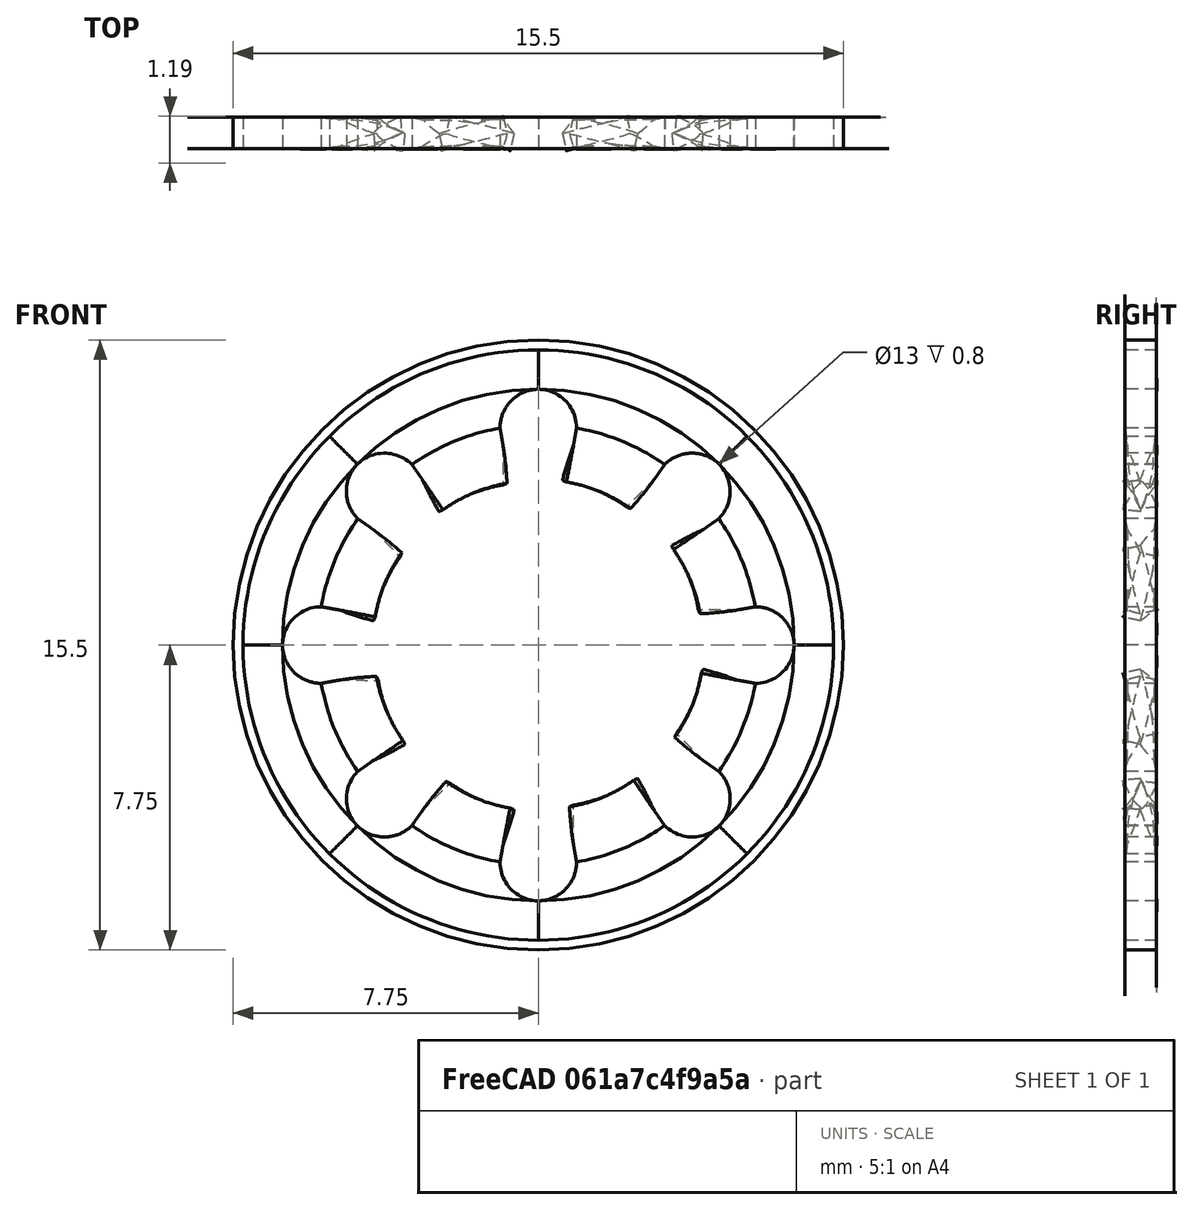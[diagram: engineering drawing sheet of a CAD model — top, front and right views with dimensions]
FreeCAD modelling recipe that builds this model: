
FCSTD DOCUMENT  (FreeCAD 0.19R24267 +99 (Git))
Label: Assembly TR Fastenings Ltd-M8 Internal Toothed Washer DIN 6797J
License: All rights reserved
LicenseURL: http://en.wikipedia.org/wiki/All_rights_reserved
objects: Part::Feature×1, Sketcher::SketchObject×1, PartDesign::Pad×1, PartDesign::Body×1
note: 5 computed .brp shape members not serialized (recipe doc carries the construction recipe); baked Part::Feature solids carry a one-line shape summary decoded from their .brp

FEATURE [Part::Feature] Part__Feature  label="TR Fastenings Ltd-M8"
  shape: bbox 19.22 x 1.686 x 19.22 mm, 104 faces, 8 solids (baked)
FEATURE [Sketcher::SketchObject] Sketch
  FullyConstrained = true
  MapMode = 5
  Placement = pos=(0,0,0) rot=(1,0,0;1.5708rad)
  Support = -> [XZ_Plane]
  sketch-geometry (2):
    g0: Circle CenterX=0 CenterY=0 CenterZ=0 NormalX=0 NormalY=0 NormalZ=1 AngleXU=0 Radius=6.5
    g1: Circle CenterX=0 CenterY=0 CenterZ=0 NormalX=0 NormalY=0 NormalZ=1 AngleXU=0 Radius=7.75
  constraints (4):
    c: Coincident(g0,g-1)
    c: Coincident(g1,g0)
    c: Diameter(g1) = 15.5
    c: Diameter(g0) = 13
FEATURE [PartDesign::Pad] Pad
  Direction = (1,1,1)
  Length = 0.8
  Length2 = 100
  Placement = pos=(0,0,0) rot=(1,0,0;1.5708rad)
  Profile = -> Sketch
  Reversed = true
  Type = 0
FEATURE [PartDesign::Body] Body
  Group = -> [Sketch,Pad]
  Origin = -> Origin
  Tip = -> Pad
